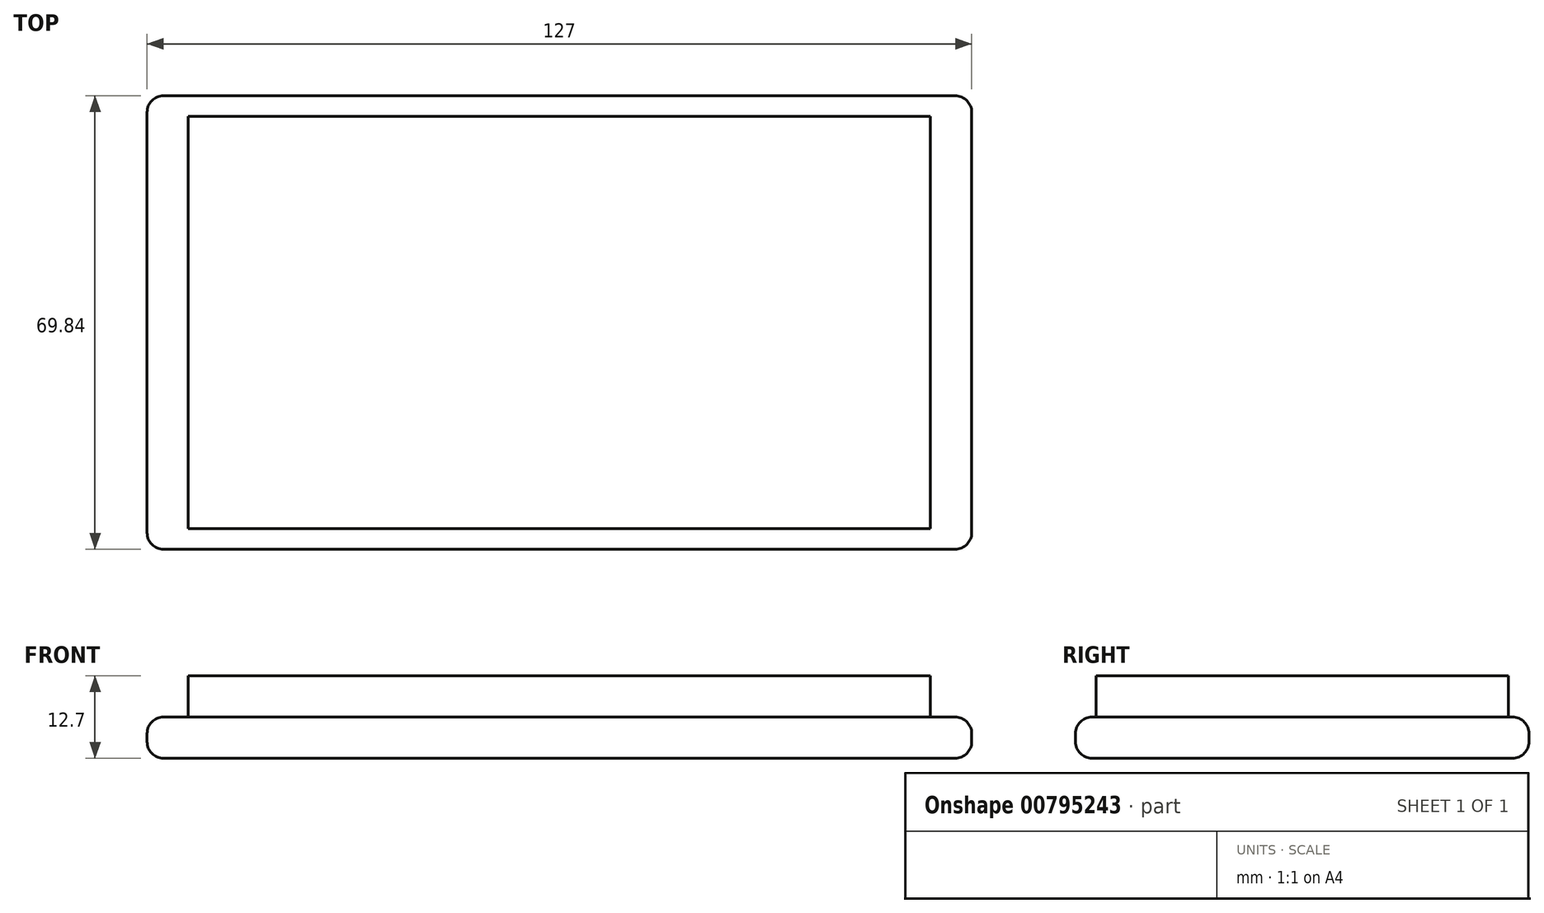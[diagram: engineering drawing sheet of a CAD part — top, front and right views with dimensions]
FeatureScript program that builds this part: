
annotation { "Feature Type Name" : "Feature", "Feature Type Description" : "" }
export const myFeature = defineFeature(function(context is Context, id is Id, definition is map)
    precondition{}
    {
        {
            var Q0;
            Q0=qCreatedBy(makeId("Top.planeOp"),FACE);
            var sketch = newSketch(context, id + "F0", { "sketchPlane" : qUnion([Q0])});
            skLineSegment(sketch, "E0.bottom", {"start": v(-63.5, 34.92) * mm, "end": v(63.5, 34.92) * mm});
            skLineSegment(sketch, "E0.top", {"start": v(-63.5, -34.92) * mm, "end": v(63.5, -34.92) * mm});
            skLineSegment(sketch, "E0.left", {"start": v(-63.5, 34.92) * mm, "end": v(-63.5, -34.92) * mm});
            skLineSegment(sketch, "E0.right", {"start": v(63.5, 34.92) * mm, "end": v(63.5, -34.92) * mm});
            skPoint(sketch, "E0.middle", {"position": v(0, 0) * mm});
            skSolve(sketch);
        }
        {
            var Q0;
            Q0=makeQuery(id+"F0.imprint","IMPRINT",FACE,{"disambiguationData":[TD([[makeQuery(id+"F0.imprint","IMPRINT",EDGE,{"derivedFrom":sQuery(id+"F0.wireOp",EDGE,"E0.bottom")}),-1.0]])]});
            extrude(context, id + "F1", {"entities" : qUnion([Q0]), "depth" : 6.35 * mm, "offsetDistance" : 25.4 * mm});
        }
        {
            var Q0;
            Q0=makeQuery(id+"F1.opExtrude","CAP_FACE",FACE,{"disambiguationData":[OSD([sQuery(id+"F0.wireOp",EDGE,"E0.bottom"),sQuery(id+"F0.wireOp",EDGE,"E0.top"),sQuery(id+"F0.wireOp",EDGE,"E0.left"),sQuery(id+"F0.wireOp",EDGE,"E0.right")])],"isStart":false});
            var sketch = newSketch(context, id + "F2", { "sketchPlane" : qUnion([Q0])});
            skLineSegment(sketch, "E1.bottom", {"start": v(-57.15, 31.75) * mm, "end": v(57.15, 31.75) * mm});
            skLineSegment(sketch, "E1.top", {"start": v(-57.15, -31.75) * mm, "end": v(57.15, -31.75) * mm});
            skLineSegment(sketch, "E1.left", {"start": v(-57.15, 31.75) * mm, "end": v(-57.15, -31.75) * mm});
            skLineSegment(sketch, "E1.right", {"start": v(57.15, 31.75) * mm, "end": v(57.15, -31.75) * mm});
            skPoint(sketch, "E1.middle", {"position": v(0, 0) * mm});
            skSolve(sketch);
        }
        {
            var Q0;
            Q0=makeQuery(id+"F2.imprint","IMPRINT",FACE,{"disambiguationData":[TD([[makeQuery(id+"F2.imprint","IMPRINT",EDGE,{"derivedFrom":sQuery(id+"F2.wireOp",EDGE,"E1.bottom")}),-1.0]])]});
            extrude(context, id + "F3", {"entities" : qUnion([Q0]), "operationType" : NewBodyOperationType.ADD, "endBound" : BoundingType.SYMMETRIC, "depth" : 12.7 * mm, "offsetDistance" : 25.4 * mm});
        }
        {
            var Q0;
            Q0=makeQuery(id+"F1.opExtrude","CAP_EDGE",EDGE,{"disambiguationData":[OSD([sQuery(id+"F0.wireOp",EDGE,"E0.top")])],"isStart":true});
            var Q1;
            Q1=makeQuery(id+"F1.opExtrude","CAP_EDGE",EDGE,{"disambiguationData":[OSD([sQuery(id+"F0.wireOp",EDGE,"E0.left")])],"isStart":true});
            var Q2;
            Q2=makeQuery(id+"F1.opExtrude","CAP_EDGE",EDGE,{"disambiguationData":[OSD([sQuery(id+"F0.wireOp",EDGE,"E0.left")])],"isStart":false});
            var Q3;
            Q3=makeQuery(id+"F1.opExtrude","SWEPT_EDGE",EDGE,{"disambiguationData":[OSD([sQuery(id+"F0.wireOp",EDGE,"E0.top"),sQuery(id+"F0.wireOp",EDGE,"E0.left")])]});
            var Q4;
            Q4=makeQuery(id+"F1.opExtrude","CAP_EDGE",EDGE,{"disambiguationData":[OSD([sQuery(id+"F0.wireOp",EDGE,"E0.top")])],"isStart":false});
            var Q5;
            Q5=makeQuery(id+"F1.opExtrude","CAP_EDGE",EDGE,{"disambiguationData":[OSD([sQuery(id+"F0.wireOp",EDGE,"E0.right")])],"isStart":true});
            var Q6;
            Q6=makeQuery(id+"F1.opExtrude","CAP_EDGE",EDGE,{"disambiguationData":[OSD([sQuery(id+"F0.wireOp",EDGE,"E0.right")])],"isStart":false});
            var Q7;
            Q7=makeQuery(id+"F1.opExtrude","SWEPT_EDGE",EDGE,{"disambiguationData":[OSD([sQuery(id+"F0.wireOp",EDGE,"E0.bottom"),sQuery(id+"F0.wireOp",EDGE,"E0.right")])]});
            var Q8;
            Q8=makeQuery(id+"F1.opExtrude","CAP_EDGE",EDGE,{"disambiguationData":[OSD([sQuery(id+"F0.wireOp",EDGE,"E0.bottom")])],"isStart":false});
            var Q9;
            Q9=makeQuery(id+"F1.opExtrude","SWEPT_EDGE",EDGE,{"disambiguationData":[OSD([sQuery(id+"F0.wireOp",EDGE,"E0.top"),sQuery(id+"F0.wireOp",EDGE,"E0.right")])]});
            var Q10;
            Q10=makeQuery(id+"F1.opExtrude","CAP_EDGE",EDGE,{"disambiguationData":[OSD([sQuery(id+"F0.wireOp",EDGE,"E0.bottom")])],"isStart":true});
            var Q11;
            Q11=makeQuery(id+"F1.opExtrude","SWEPT_EDGE",EDGE,{"disambiguationData":[OSD([sQuery(id+"F0.wireOp",EDGE,"E0.bottom"),sQuery(id+"F0.wireOp",EDGE,"E0.left")])]});
            fillet(context, id + "F4", {"entities" : qUnion([Q0, Q1, Q2, Q3, Q4, Q5, Q6, Q7, Q8, Q9, Q10, Q11]), "radius" : 2.54 * mm, "tangentPropagation" : true, "allowEdgeOverflow" : false});
        }
    });
